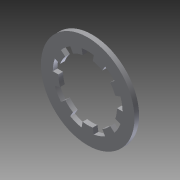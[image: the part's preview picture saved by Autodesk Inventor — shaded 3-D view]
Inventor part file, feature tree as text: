
AUTODESK INVENTOR PART (.ipt)
format: ipt  version: 2011 SP1 (Build 150282100, 282)  size: 117,248 bytes
history: native  units: in
note: dims shown in document units (in); Inventor stores cm internally (conversion verified against a paired STEP export)
features: other x7, extrude x1, sketch x1
ambient origin geometry x8: Origin, YZ Plane, XZ Plane, XY Plane, X Axis, Y Axis, Z Axis, Center Point
bodies: Solid1 (feature_tree)
feature tree (9):
  extrude  "Extrusion1"  [1 undecoded]
  other  "lockwasher_XY"
  other  "lockwasher_YZ"
  other  "lockwasher_ZX"
  other  "lockwasher_X"
  other  "lockwasher_Y"
  other  "lockwasher_Z"
  other  "lockwasher_Center"
  sketch  "Sketch_2"  dims[d0=0.02in d1=0.0in]
note: 1 required parameter value undecoded (feature->parameter linkage not recoverable at this tier; creation-order binding heuristic only, values carry confidence <= 0.55)
